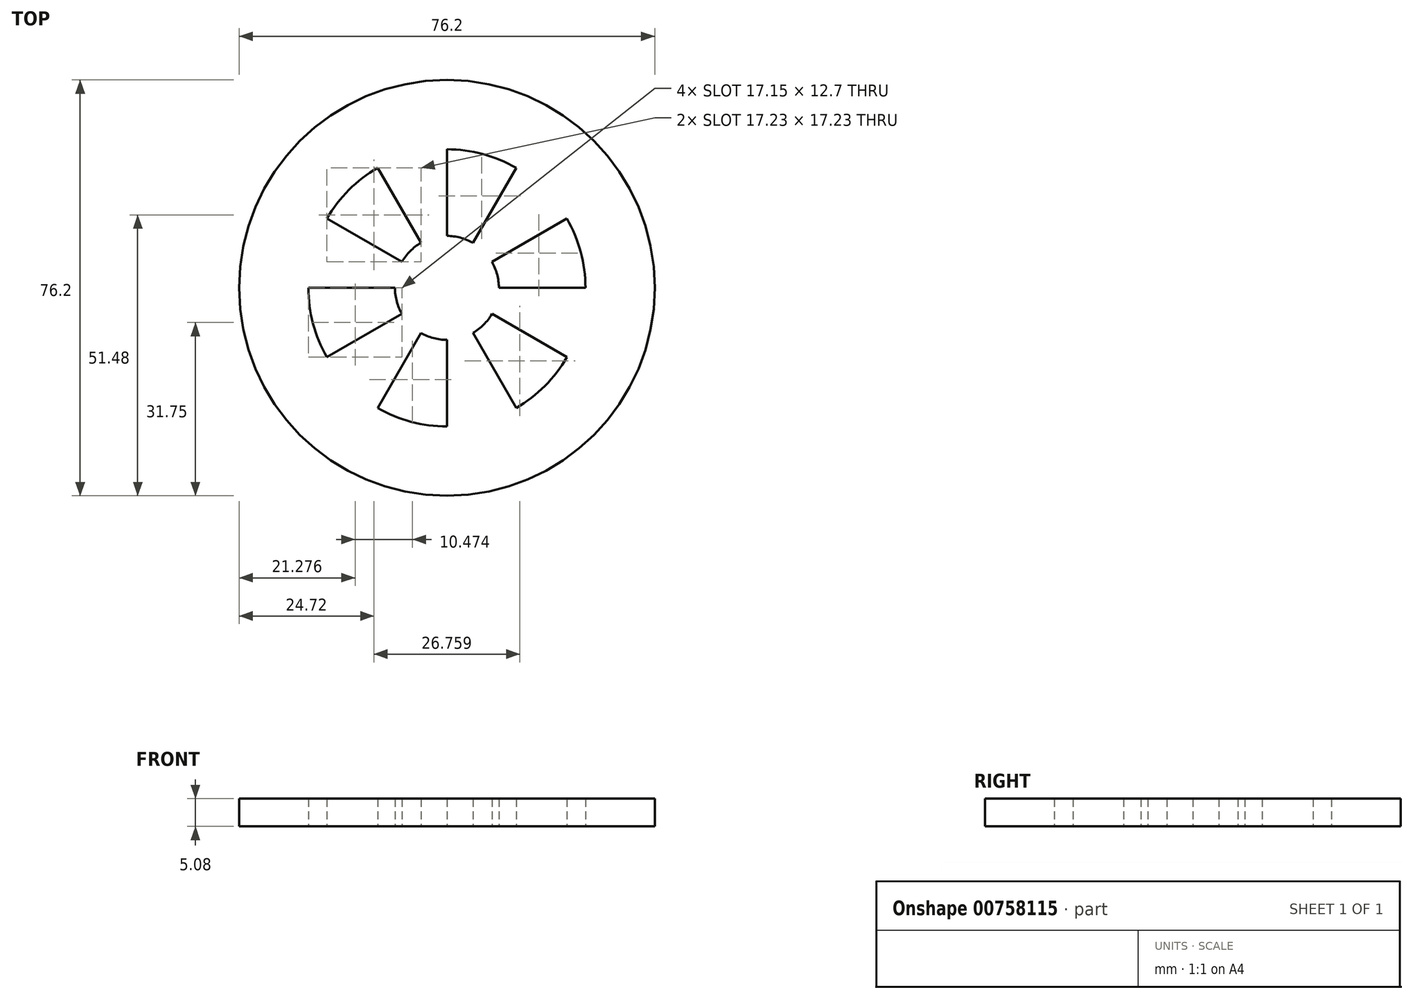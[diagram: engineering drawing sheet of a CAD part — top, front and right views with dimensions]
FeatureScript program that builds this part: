
annotation { "Feature Type Name" : "Feature", "Feature Type Description" : "" }
export const myFeature = defineFeature(function(context is Context, id is Id, definition is map)
    precondition{}
    {
        {
            var Q0;
            Q0=qCreatedBy(makeId("Top.planeOp"),FACE);
            var sketch = newSketch(context, id + "F0", { "sketchPlane" : qUnion([Q0])});
            skCircle(sketch, "E0", {"center": v(0, 0) * mm, "radius": 38.1 * mm});
            skCircle(sketch, "E1", {"center": v(0, 0) * mm, "radius": 25.4 * mm});
            skLineSegment(sketch, "E2", {"start": v(0, 0) * mm, "end": v(25.4, 0) * mm});
            skLineSegment(sketch, "E3", {"start": v(0, 0) * mm, "end": v(22, 12.7) * mm});
            skLineSegment(sketch, "E4", {"start": v(0, 0) * mm, "end": v(12.7, 22) * mm});
            skLineSegment(sketch, "E5", {"start": v(0, 0) * mm, "end": v(0, 25.4) * mm});
            skLineSegment(sketch, "E6", {"start": v(0, 0) * mm, "end": v(-12.7, 22) * mm});
            skLineSegment(sketch, "E7", {"start": v(0, 0) * mm, "end": v(-22, 12.7) * mm});
            skLineSegment(sketch, "E8", {"start": v(0, 0) * mm, "end": v(-25.4, 0) * mm});
            skLineSegment(sketch, "E9", {"start": v(0, 0) * mm, "end": v(-22, -12.7) * mm});
            skLineSegment(sketch, "E10", {"start": v(0, 0) * mm, "end": v(-12.7, -22) * mm});
            skLineSegment(sketch, "E11", {"start": v(0, 0) * mm, "end": v(0, -25.4) * mm});
            skLineSegment(sketch, "E12", {"start": v(0, 0) * mm, "end": v(12.7, -22) * mm});
            skLineSegment(sketch, "E13", {"start": v(0, 0) * mm, "end": v(22, -12.7) * mm});
            skCircle(sketch, "E14", {"center": v(0, 0) * mm, "radius": 9.53 * mm});
            skSolve(sketch);
        }
        {
            var Q0;
            Q0=makeQuery(id+"F0.imprint","IMPRINT",FACE,{"disambiguationData":[TD([[makeQuery(id+"F0.imprint","IMPRINT",EDGE,{"derivedFrom":sQuery(id+"F0.wireOp",EDGE,"E0")}),1.0]])]});
            var Q1;
            {var subQ1=sQuery(id+"F0.wireOp",EDGE,"E8");var subQ3=sQuery(id+"F0.wireOp",EDGE,"E14");var subQ4=makeQuery(id+"F0.imprint","INTERSECT",VERTEX,{"derivedFrom":[subQ1,subQ3]});Q1=makeQuery(id+"F0.imprint","IMPRINT",FACE,{"disambiguationData":[TD([[makeQuery(id+"F0.imprint","IMPRINT",EDGE,{"disambiguationData":[TD([[subQ4,-1.0]])],"derivedFrom":subQ3}),1.0]])]});}
            var Q2;
            {var subQ1=sQuery(id+"F0.wireOp",EDGE,"E9");var subQ3=sQuery(id+"F0.wireOp",EDGE,"E14");var subQ4=makeQuery(id+"F0.imprint","INTERSECT",VERTEX,{"derivedFrom":[subQ1,subQ3]});Q2=makeQuery(id+"F0.imprint","IMPRINT",FACE,{"disambiguationData":[TD([[makeQuery(id+"F0.imprint","IMPRINT",EDGE,{"disambiguationData":[TD([[subQ4,-1.0]])],"derivedFrom":subQ3}),1.0]])]});}
            var Q3;
            {var subQ1=sQuery(id+"F0.wireOp",EDGE,"E10");var subQ3=sQuery(id+"F0.wireOp",EDGE,"E14");var subQ4=makeQuery(id+"F0.imprint","INTERSECT",VERTEX,{"derivedFrom":[subQ1,subQ3]});Q3=makeQuery(id+"F0.imprint","IMPRINT",FACE,{"disambiguationData":[TD([[makeQuery(id+"F0.imprint","IMPRINT",EDGE,{"disambiguationData":[TD([[subQ4,-1.0]])],"derivedFrom":subQ3}),1.0]])]});}
            var Q4;
            {var subQ1=sQuery(id+"F0.wireOp",EDGE,"E11");var subQ3=sQuery(id+"F0.wireOp",EDGE,"E14");var subQ4=makeQuery(id+"F0.imprint","INTERSECT",VERTEX,{"derivedFrom":[subQ1,subQ3]});Q4=makeQuery(id+"F0.imprint","IMPRINT",FACE,{"disambiguationData":[TD([[makeQuery(id+"F0.imprint","IMPRINT",EDGE,{"disambiguationData":[TD([[subQ4,-1.0]])],"derivedFrom":subQ3}),1.0]])]});}
            var Q5;
            {var subQ1=sQuery(id+"F0.wireOp",EDGE,"E12");var subQ3=sQuery(id+"F0.wireOp",EDGE,"E14");var subQ4=makeQuery(id+"F0.imprint","INTERSECT",VERTEX,{"derivedFrom":[subQ1,subQ3]});Q5=makeQuery(id+"F0.imprint","IMPRINT",FACE,{"disambiguationData":[TD([[makeQuery(id+"F0.imprint","IMPRINT",EDGE,{"disambiguationData":[TD([[subQ4,-1.0]])],"derivedFrom":subQ3}),1.0]])]});}
            var Q6;
            {var subQ1=sQuery(id+"F0.wireOp",EDGE,"E2");var subQ3=sQuery(id+"F0.wireOp",EDGE,"E14");var subQ4=makeQuery(id+"F0.imprint","INTERSECT",VERTEX,{"derivedFrom":[subQ1,subQ3]});Q6=makeQuery(id+"F0.imprint","IMPRINT",FACE,{"disambiguationData":[TD([[makeQuery(id+"F0.imprint","IMPRINT",EDGE,{"disambiguationData":[TD([[subQ4,1.0]])],"derivedFrom":subQ3}),1.0]])]});}
            var Q7;
            {var subQ1=sQuery(id+"F0.wireOp",EDGE,"E2");var subQ3=sQuery(id+"F0.wireOp",EDGE,"E14");var subQ4=makeQuery(id+"F0.imprint","INTERSECT",VERTEX,{"derivedFrom":[subQ1,subQ3]});Q7=makeQuery(id+"F0.imprint","IMPRINT",FACE,{"disambiguationData":[TD([[makeQuery(id+"F0.imprint","IMPRINT",EDGE,{"disambiguationData":[TD([[subQ4,-1.0]])],"derivedFrom":subQ3}),1.0]])]});}
            var Q8;
            {var subQ1=sQuery(id+"F0.wireOp",EDGE,"E3");var subQ3=sQuery(id+"F0.wireOp",EDGE,"E14");var subQ4=makeQuery(id+"F0.imprint","INTERSECT",VERTEX,{"derivedFrom":[subQ1,subQ3]});Q8=makeQuery(id+"F0.imprint","IMPRINT",FACE,{"disambiguationData":[TD([[makeQuery(id+"F0.imprint","IMPRINT",EDGE,{"disambiguationData":[TD([[subQ4,-1.0]])],"derivedFrom":subQ3}),1.0]])]});}
            var Q9;
            {var subQ1=sQuery(id+"F0.wireOp",EDGE,"E4");var subQ3=sQuery(id+"F0.wireOp",EDGE,"E14");var subQ4=makeQuery(id+"F0.imprint","INTERSECT",VERTEX,{"derivedFrom":[subQ1,subQ3]});Q9=makeQuery(id+"F0.imprint","IMPRINT",FACE,{"disambiguationData":[TD([[makeQuery(id+"F0.imprint","IMPRINT",EDGE,{"disambiguationData":[TD([[subQ4,-1.0]])],"derivedFrom":subQ3}),1.0]])]});}
            var Q10;
            {var subQ1=sQuery(id+"F0.wireOp",EDGE,"E5");var subQ3=sQuery(id+"F0.wireOp",EDGE,"E14");var subQ4=makeQuery(id+"F0.imprint","INTERSECT",VERTEX,{"derivedFrom":[subQ1,subQ3]});Q10=makeQuery(id+"F0.imprint","IMPRINT",FACE,{"disambiguationData":[TD([[makeQuery(id+"F0.imprint","IMPRINT",EDGE,{"disambiguationData":[TD([[subQ4,-1.0]])],"derivedFrom":subQ3}),1.0]])]});}
            var Q11;
            {var subQ1=sQuery(id+"F0.wireOp",EDGE,"E6");var subQ3=sQuery(id+"F0.wireOp",EDGE,"E14");var subQ4=makeQuery(id+"F0.imprint","INTERSECT",VERTEX,{"derivedFrom":[subQ1,subQ3]});Q11=makeQuery(id+"F0.imprint","IMPRINT",FACE,{"disambiguationData":[TD([[makeQuery(id+"F0.imprint","IMPRINT",EDGE,{"disambiguationData":[TD([[subQ4,-1.0]])],"derivedFrom":subQ3}),1.0]])]});}
            var Q12;
            {var subQ1=sQuery(id+"F0.wireOp",EDGE,"E7");var subQ3=sQuery(id+"F0.wireOp",EDGE,"E14");var subQ4=makeQuery(id+"F0.imprint","INTERSECT",VERTEX,{"derivedFrom":[subQ1,subQ3]});Q12=makeQuery(id+"F0.imprint","IMPRINT",FACE,{"disambiguationData":[TD([[makeQuery(id+"F0.imprint","IMPRINT",EDGE,{"disambiguationData":[TD([[subQ4,-1.0]])],"derivedFrom":subQ3}),1.0]])]});}
            var Q13;
            {var subQ0=sQuery(id+"F0.wireOp",EDGE,"E7");var subQ1=sQuery(id+"F0.wireOp",EDGE,"E1");var subQ2=makeQuery(id+"F0.imprint","INTERSECT",VERTEX,{"derivedFrom":[subQ1,subQ0]});Q13=makeQuery(id+"F0.imprint","IMPRINT",FACE,{"disambiguationData":[TD([[makeQuery(id+"F0.imprint","IMPRINT",EDGE,{"disambiguationData":[TD([[subQ2,-1.0]])],"derivedFrom":subQ1}),1.0]])]});}
            var Q14;
            {var subQ0=sQuery(id+"F0.wireOp",EDGE,"E5");var subQ1=sQuery(id+"F0.wireOp",EDGE,"E1");var subQ2=makeQuery(id+"F0.imprint","INTERSECT",VERTEX,{"derivedFrom":[subQ1,subQ0]});Q14=makeQuery(id+"F0.imprint","IMPRINT",FACE,{"disambiguationData":[TD([[makeQuery(id+"F0.imprint","IMPRINT",EDGE,{"disambiguationData":[TD([[subQ2,-1.0]])],"derivedFrom":subQ1}),1.0]])]});}
            var Q15;
            {var subQ0=sQuery(id+"F0.wireOp",EDGE,"E3");var subQ1=sQuery(id+"F0.wireOp",EDGE,"E1");var subQ2=makeQuery(id+"F0.imprint","INTERSECT",VERTEX,{"derivedFrom":[subQ1,subQ0]});Q15=makeQuery(id+"F0.imprint","IMPRINT",FACE,{"disambiguationData":[TD([[makeQuery(id+"F0.imprint","IMPRINT",EDGE,{"disambiguationData":[TD([[subQ2,-1.0]])],"derivedFrom":subQ1}),1.0]])]});}
            var Q16;
            {var subQ0=sQuery(id+"F0.wireOp",EDGE,"E2");var subQ1=sQuery(id+"F0.wireOp",EDGE,"E1");var subQ2=makeQuery(id+"F0.imprint","INTERSECT",VERTEX,{"derivedFrom":[subQ1,subQ0]});Q16=makeQuery(id+"F0.imprint","IMPRINT",FACE,{"disambiguationData":[TD([[makeQuery(id+"F0.imprint","IMPRINT",EDGE,{"disambiguationData":[TD([[subQ2,1.0]])],"derivedFrom":subQ1}),1.0]])]});}
            var Q17;
            {var subQ0=sQuery(id+"F0.wireOp",EDGE,"E11");var subQ1=sQuery(id+"F0.wireOp",EDGE,"E1");var subQ2=makeQuery(id+"F0.imprint","INTERSECT",VERTEX,{"derivedFrom":[subQ1,subQ0]});Q17=makeQuery(id+"F0.imprint","IMPRINT",FACE,{"disambiguationData":[TD([[makeQuery(id+"F0.imprint","IMPRINT",EDGE,{"disambiguationData":[TD([[subQ2,-1.0]])],"derivedFrom":subQ1}),1.0]])]});}
            var Q18;
            {var subQ0=sQuery(id+"F0.wireOp",EDGE,"E9");var subQ1=sQuery(id+"F0.wireOp",EDGE,"E1");var subQ2=makeQuery(id+"F0.imprint","INTERSECT",VERTEX,{"derivedFrom":[subQ1,subQ0]});Q18=makeQuery(id+"F0.imprint","IMPRINT",FACE,{"disambiguationData":[TD([[makeQuery(id+"F0.imprint","IMPRINT",EDGE,{"disambiguationData":[TD([[subQ2,-1.0]])],"derivedFrom":subQ1}),1.0]])]});}
            extrude(context, id + "F1", {"entities" : qUnion([Q0, Q1, Q2, Q3, Q4, Q5, Q6, Q7, Q8, Q9, Q10, Q11, Q12, Q13, Q14, Q15, Q16, Q17, Q18]), "depth" : 5.08 * mm, "offsetDistance" : 25.4 * mm});
        }
    });
